# Revit family: QF_ELECTROLUXPROFESSIONAL_1LSN7S_WB6-20_E
name_source: partatom
category: Attrezzature speciali
units: mm (PartAtom-declared; Revit-internal decimal feet)

## family parameters
Basato su piano di lavoro = No
Condiviso = No
Punto di calcolo locali = No
Quota connettore circolare = Usa diametro
Sempre verticale = Sì
Taglio con vuoti quando caricato = No
Tipo di parte = Normale

## types (108) — shared parameters
Cold Water Maximum Pressure = 0.00 psi
Cold Water Minimum Pressure = 0.00 psi
Cold Water Size = 1"
Conn Conduit = Sì
Depth Actual = 1050 mm
Electrical Remarks = 400 V/3N ph/50/60 Hz
Height Actual = 1640 mm  [stored 5.38058 ft]
Hot Water Consumption = 0 GPM
Hot Water Maximum Pressure = 0.00 psi
Hot Water Minimum Pressure = 0.00 psi
Hot Water Size = 1"
Hot Water Temperature = -460 °F
Indirect Waste Size = 1"
Latent Heat Output = 0.0
Length Actual = 915 mm  [stored 3.00197 ft]
Max Overcurrent Protection = 0 A
Min Ckt Ampacity = 0 A
Modello = WB6-20
Phase = 3
Produttore = Electrolux Professional
Sensible Heat Output = 0.0
URL = www.electroluxprofessional.com
Weight = 670
Weight in Pounds = 55.1
zero-valued in all types: Cold Water Connection Height, Gas KW, Hot Water Connection Height, Indirect Waste Connection Height, Prospetto di default, Steam Pounds per Hour

## per-type parameters (varying)
| type | Descrizione | Volts | Watts |
| 9890030056 | WASHER WB6-20 200L 2DOORS RIGHT/RIGHT EL. 380-415/50/60/3 2xCOMPASS PRO 2xWATER 13xLIQ. SILVER TAP BMP | 415 V | 15000 W |
| 9890030096 | WASHER WB6-20 200L 2DOORS RIGHT/RIGHT EL. 380-415/50/60/3 COMPASS PRO 2xWATER 13xLIQ. SILVER IWS TAP EXP. | 415 V | 15000 W |
| 9890030086 | WASHER WB6-20 200L 2DOORS RIGHT/RIGHT EL. 380-415/50/60/3 2xCOMPASS PRO 2xWATER 13xLIQ. SST IWS | 415 V | 15000 W |
| 9890030052 | WASHER WB6-20 200L 2DOORS RIGHT/LEFT EL. 380-415/50/60/3 COMPASS PRO 2xWATER 13xLIQ. SILVER EXP. | 415 V | 15000 W |
| 9890030042 | WASHER WB6-20 200L 2DOORS RIGHT/RIGHT EL. 380-415/50/60/3 COMPASS PRO 3xWATER 13xLIQ.+POWDER SILVER BMP | 415 V | 15000 W |
| 9890030072 | WASHER WB6-20 200L 2DOORS LEFT/RIGHT EL. 380-415/50/60/3 COMPASS PRO 2xWATER 13xLIQ. SILVER TAP ALARM EXP. | 415 V | 15000 W |
| 9890030062 | WASHER WB6-20 200L 2DOORS RIGHT/RIGHT EL. 380-415/50/60/3 2xCOMPASS PRO 3xWATER 13xLIQ. SILVER TAP ALARM | 415 V | 15000 W |
| 9890030012 | WASHER WB6-20 200L 2DOORS RIGHT/RIGHT EL. 230/50/60/3 2xCOMPASS PRO 2xWATER 13xLIQ. SILVER AIDO TAP ALARM EXP. | 230 V | 15000 W |
| 9890030002 | WASHER WB6-20 200L 2DOORS RIGHT/RIGHT EL. 380-415/50/60/3 2xCOMPASS PRO 3xWATER 13xLIQ. SILVER ALARM EXP. | 415 V | 15000 W |
| 9890030032 | WASHER WB6-20 200L 2DOORS RIGHT/RIGHT EL. 380-415/50/60/3 COMPASS PRO 3xWATER 13xLIQ. SILVER | 415 V | 15000 W |
| 9890030022 | WASHER WB6-20 200L 2DOORS RIGHT/RIGHT EL. 230/50/60/3 2xCOMPASS PRO 2xWATER 13xLIQ. SILVER TAP ALARM EXP. | 230 V | 15000 W |
| 9890030082 | WASHER WB6-20 200L 2DOORS RIGHT/RIGHT EL. 380-415/50/60/3 2xCOMPASS PRO 2xWATER 13xLIQ.+POWDER SILVER EXP. | 415 V | 15000 W |
| 9890030114 | WASHER WB6-20 200L 2DOORS LEFT/LEFT EL. 380-415/50/60/3 COMPASS PRO 3xWATER 13xLIQ.+POWDER SILVER IWS ALARM EXP. | 415 V | 15000 W |
| 9890030104 | WASHER WB6-20 200L 2DOORS RIGHT/RIGHT EL. 380-415/50/60/3 2xCOMPASS PRO 3xWATER 13xLIQ.+POWDER SILVER AIDO TAP ALARM EXP | 415 V | 15000 W |
| 9890030079 | WASHER WB6-20 200L 2DOORS LEFT/RIGHT EL. 380-415/50/60/3 COMPASS PRO 2xWATER 13xLIQ. SILVER ALARM | 415 V | 15000 W |
| 9890030049 | WASHER WB6-20 200L 2DOORS RIGHT/RIGHT EL. 380-415/50/60/3 2xCOMPASS PRO 3xWATER 13xLIQ. SILVER AIDO ALARM | 415 V | 15000 W |
| 9890030019 | WASHER WB6-20 200L 2DOORS LEFT/LEFT EL. 380-415/50/60/3 COMPASS PRO 2xWATER 13xLIQ. SILVER | 415 V | 15000 W |
| 9890030009 | WASHER WB6-20 200L 2DOORS RIGHT/RIGHT EL. 380-415/50/60/3 2xCOMPASS PRO 2xWATER 13xLIQ. SILVER EXP. | 415 V | 15000 W |
| 9890030039 | WASHER WB6-20 200L 2DOORS RIGHT/LEFT EL. 380-415/50/60/3 2xCOMPASS PRO 2xWATER 13xLIQ. SILVER ALARM EXP. | 415 V | 15000 W |
| 9890030059 | WASHER WB6-20 200L 2DOORS RIGHT/RIGHT EL. 380-415/50/60/3 2xCOMPASS PRO 3xWATER 13xLIQ.+POWDER SILVER | 415 V | 15000 W |
| 9890030069 | WASHER WB6-20 200L 2DOORS LEFT/RIGHT EL. 380-415/50/60/3 COMPASS PRO 3xWATER 13xLIQ.+POWDER SILVER EXP. | 415 V | 15000 W |
| 9890030099 | WASHER WB6-20 200L 2DOORS RIGHT/RIGHT EL. 380-415/50/60/3 2xCOMPASS PRO 2xWATER 13xLIQ. SILVER AIDO IWS TAP ALARM EXP. | 415 V | 15000 W |
| 9890030089 | WASHER WB6-20 200L 2DOORS RIGHT/RIGHT EL. 380-415/50/60/3 COMPASS PRO 2xWATER 13xLIQ.+POWDER SILVER ALARM EXP. | 415 V | 15000 W |
| 9890030055 | WASHER WB6-20 200L 2DOORS RIGHT/RIGHT NO HEATING 380-415/50/60/3 COMPASS PRO 2xWATER 13xLIQ. SILVER | 415 V | 6000 W |
| 9890030045 | WASHER WB6-20 200L 2DOORS RIGHT/RIGHT EL. 380-415/50/60/3 2xCOMPASS PRO 3xWATER 13xLIQ. SILVER AIDO | 415 V | 15000 W |
| 9890030075 | WASHER WB6-20 200L 2DOORS RIGHT/RIGHT EL. 380-415/50/60/3 2xCOMPASS PRO 2xWATER 13xLIQ. SILVER AIDO ALARM | 415 V | 15000 W |
| 9890030065 | WASHER WB6-20 200L 2DOORS RIGHT/RIGHT EL. 380-415/50/60/3 2xCOMPASS PRO 2xWATER 13xLIQ.+POWDER SILVER TAP ALARM | 415 V | 15000 W |
| 9890030015 | WASHER WB6-20 200L 2DOORS RIGHT/RIGHT EL. 380-415/50/60/3 2xCOMPASS PRO 2xWATER 13xLIQ. SILVER AIDO | 415 V | 15000 W |
| 9890030005 | WASHER WB6-20 200L 2DOORS RIGHT/RIGHT EL. 380-415/50/60/3 COMPASS PRO 2xWATER 13xLIQ. SILVER | 415 V | 15000 W |
| 9890030035 | WASHER WB6-20 200L 2DOORS RIGHT/RIGHT EL. 380-415/50/60/3 COMPASS PRO 2xWATER 13xLIQ.+POWDER SILVER | 415 V | 15000 W |
| 9890030025 | WASHER WB6-20 200L 2DOORS LEFT/RIGHT EL. 380-415/50/60/3 COMPASS PRO 2xWATER 13xLIQ. SILVER TAP EXP. | 415 V | 15000 W |
| 9890030100 | WASHER WB6-20 200L 2DOORS RIGHT/RIGHT EL. 380-415/50/60/3 2xCOMPASS PRO 2xWATER 13xLIQ. SILVER IWS ALARM | 415 V | 15000 W |
| 9890030110 | WASHER WB6-20 200L 2DOORS RIGHT/RIGHT EL. 380-415/50/60/3 COMPASS PRO 2xWATER 13xLIQ. SILVER IWS | 415 V | 15000 W |
| 9890030085 | WASHER WB6-20 200L 2DOORS RIGHT/RIGHT EL. 380-415/50/60/3 2xCOMPASS PRO 2xWATER 13xLIQ.+POWDER SILVER ALARM EXP. | 415 V | 15000 W |
| 9890030058 | WASHER WB6-20 200L 2DOORS RIGHT/RIGHT EL. 380-415/50/60/3 2xCOMPASS PRO 2xWATER 13xLIQ. SILVER IWS ALARM BMP EXP. | 415 V | 15000 W |
| 9890030048 | WASHER WB6-20 200L 2DOORS LEFT/RIGHT EL. 380-415/50/60/3 2xCOMPASS PRO 2xWATER 13xLIQ.+POWDER SILVER | 415 V | 15000 W |
| 9890030078 | WASHER WB6-20 200L 2DOORS RIGHT/RIGHT EL. 380-415/50/60/3 2xCOMPASS PRO 2xWATER 13xLIQ.+POWDER SILVER IWS BMP | 415 V | 15000 W |
| 9890030068 | WASHER WB6-20 200L 2DOORS RIGHT/RIGHT EL. 380-415/50/60/3 2xCOMPASS PRO 2xWATER 13xLIQ. SILVER ALARM | 415 V | 15000 W |
| 9890030018 | WASHER WB6-20 200L 2DOORS LEFT/RIGHT EL. 380-415/50/60/3 COMPASS PRO 2xWATER 13xLIQ. SILVER | 415 V | 15000 W |
| 9890030008 | WASHER WB6-20 200L 2DOORS RIGHT/RIGHT EL. 380-415/50/60/3 2xCOMPASS PRO 2xWATER 13xLIQ. SILVER ALARM EXP. | 415 V | 15000 W |
| 9890030038 | WASHER WB6-20 200L 2DOORS LEFT/LEFT EL. 380-415/50/60/3 2xCOMPASS PRO 3xWATER 13xLIQ.+POWDER 2xDRAIN SILVER TAP ALARM EX | 415 V | 15000 W |
| 9890030028 | WASHER WB6-20 200L 2DOORS RIGHT/RIGHT EL. 380-415/50/60/3 COMPASS PRO 2xWATER 13xLIQ.+POWDER SILVER EXP. | 415 V | 15000 W |
| 9890030115 | WASHER WB6-20 200L 2DOORS RIGHT/RIGHT EL. 380-415/50/60/3 2xCOMPASS PRO 2xWATER 13xLIQ. SILVER ALARM BMP EXP. | 415 V | 15000 W |
| 9890030098 | WASHER WB6-20 200L 2DOORS RIGHT/RIGHT EL. 380-415/50/60/3 2xCOMPASS PRO 3xWATER 13xLIQ.+POWDER SST IWS ALARM EXP. | 415 V | 15000 W |
| 9890030088 | WASHER WB6-20 200L 2DOORS RIGHT/RIGHT EL. 380-415/50/60/3 COMPASS PRO 2xWATER 13xLIQ.+POWDER SILVER EXP. | 415 V | 15000 W |
| 9890030051 | WASHER WB6-20 200L 2DOORS LEFT/LEFT EL. 380-415/50/60/3 2xCOMPASS PRO 2xWATER 13xLIQ.+POWDER SST ALARM EXP. | 415 V | 15000 W |
| 9890030071 | WASHER WB6-20 200L 2DOORS RIGHT/LEFT EL. 380-415/50/60/3 COMPASS PRO 2xWATER 13xLIQ. SILVER TAP ALARM EXP. | 415 V | 15000 W |
| 9890030061 | WASHER WB6-20 200L 2DOORS RIGHT/RIGHT EL. 380-415/50/60/3 2xCOMPASS PRO 3xWATER 13xLIQ.+POWDER SILVER AIDO ALARM EXP. | 415 V | 15000 W |
| 9890030011 | WASHER WB6-20 200L 2DOORS RIGHT/RIGHT EL. 230/50/60/3 2xCOMPASS PRO 2xWATER 13xLIQ. SILVER TAP ALARM EXP. | 230 V | 15000 W |
| 9890030001 | WB6-20 EL GR CP 400/3/50 | 415 V | 15000 W |
| 9890030031 | WASHER WB6-20 200L 2DOORS RIGHT/RIGHT NO HEATING 380-415/50/60/3 2xCOMPASS PRO 3xWATER 13xLIQ. 2xDRAIN SILVER AIDO TAP A | 415 V | 6000 W |
| 9890030021 | WASHER WB6-20 200L 2DOORS RIGHT/RIGHT EL. 380-415/50/60/3 2xCOMPASS PRO 2xWATER 13xLIQ.+POWDER SILVER IWS ALARM EXP. | 415 V | 15000 W |
| 9890030081 | WASHER WB6-20 200L 2DOORS RIGHT/RIGHT EL. 380-415/50/60/3 2xCOMPASS PRO 2xWATER 13xLIQ. SILVER IWS | 415 V | 15000 W |
| 9890030091 | WASHER WB6-20 200L 2DOORS RIGHT/RIGHT EL. 380-415/50/60/3 2xCOMPASS PRO 2xWATER 13xLIQ.+POWDER SST AIDO ALARM EXP. | 415 V | 15000 W |
| 9890030054 | WASHER WB6-20 200L 2DOORS RIGHT/LEFT EL. 380-415/50/60/3 2xCOMPASS PRO 2xWATER 13xLIQ. SILVER | 415 V | 15000 W |
| 9890030044 | WASHER WB6-20 200L 2DOORS RIGHT/LEFT EL. 380-415/50/60/3 COMPASS PRO 3xWATER 13xLIQ. SILVER | 415 V | 15000 W |
| 9890030074 | WASHER WB6-20 200L 2DOORS RIGHT/RIGHT EL. 380-415/50/60/3 2xCOMPASS PRO 2xWATER 13xLIQ. SILVER AIDO IWS ALARM EXP. | 415 V | 15000 W |
| 9890030064 | WASHER WB6-20 200L 2DOORS RIGHT/RIGHT EL. 380-415/50/60/3 2xCOMPASS PRO 2xWATER 13xLIQ. SILVER TAP ALARM | 415 V | 15000 W |
| 9890030014 | WASHER WB6-20 200L 2DOORS RIGHT/RIGHT EL. 380-415/50/60/3 2xCOMPASS PRO 2xWATER 13xLIQ. SILVER AIDO TAP ALARM EXP. | 415 V | 15000 W |
| 9890030004 | WASHER WB6-20 200L 2DOORS LEFT/RIGHT EL. 380-415/50/60/3 COMPASS PRO 2xWATER 13xLIQ.+POWDER SILVER EXP. | 415 V | 15000 W |
| 9893030002 | WASHER WB6-20 200L 2DOORS RIGHT/RIGHT NO HEATING 208-240/50/60/3 COMPASS PRO 2xWATER 13xLIQ.+POWDER SILVER ALARM EXP. ET | 240 V | 6000 W |
| 9890030024 | WASHER WB6-20 200L 2DOORS RIGHT/RIGHT NO HEATING 380-415/50/60/3 2xCOMPASS PRO 3xWATER 13xLIQ. 2xDRAIN SILVER AIDO TAP A | 415 V | 6000 W |
| 9890030101 | WASHER WB6-20 200L 2DOORS RIGHT/RIGHT EL. 380-415/50/60/3 COMPASS PRO 2xWATER 13xLIQ. SILVER TAP ALARM | 415 V | 15000 W |
| 9890030084 | WASHER WB6-20 200L 2DOORS RIGHT/RIGHT EL. 380-415/50/60/3 COMPASS PRO 2xWATER 13xLIQ. SILVER TAP ALARM EXP. | 415 V | 15000 W |
| 9890030050 | WASHER WB6-20 200L 2DOORS RIGHT/LEFT EL. 380-415/50/60/3 COMPASS PRO 2xWATER 13xLIQ.+POWDER SILVER EXP. | 415 V | 15000 W |
| 9890030040 | WASHER WB6-20 200L 2DOORS RIGHT/RIGHT EL. 380-415/50/60/3 2xCOMPASS PRO 2xWATER 13xLIQ. SILVER ALARM EXP. | 415 V | 15000 W |
| 9890030070 | WASHER WB6-20 200L 2DOORS RIGHT/LEFT EL. 380-415/50/60/3 2xCOMPASS PRO 2xWATER 13xLIQ. SILVER ALARM EXP. | 415 V | 15000 W |
| 9890030060 | WASHER WB6-20 200L 2DOORS LEFT/LEFT EL. 380-415/50/60/3 2xCOMPASS PRO 2xWATER 13xLIQ.+POWDER SILVER | 415 V | 15000 W |
| 9890030010 | WASHER WB6-20 200L 2DOORS RIGHT/RIGHT EL. 380-415/50/60/3 COMPASS PRO 3xWATER 13xLIQ.+POWDER SILVER EXP. | 415 V | 15000 W |
| 9890030030 | WASHER WB6-20 200L 2DOORS RIGHT/RIGHT EL. 380-415/50/60/3 2xCOMPASS PRO 3xWATER 13xLIQ.+POWDER 2xDRAIN SILVER AIDO TAP A | 415 V | 15000 W |
| 9890030020 | WASHER WB6-20 200L 2DOORS LEFT/RIGHT EL. 380-415/50/60/3 COMPASS PRO 2xWATER 13xLIQ. SILVER EXP. | 415 V | 15000 W |
| 9890030080 | WASHER WB6-20 200L 2DOORS LEFT/RIGHT EL. 380-415/50/60/3 2xCOMPASS PRO 2xWATER 13xLIQ. SILVER TAP ALARM EXP. | 415 V | 15000 W |
| 9893030003 | WASHER WB6-20 200L 2DOORS RIGHT/RIGHT EL. 208-240/50/60/3 COMPASS PRO 2xWATER 13xLIQ.+POWDER SILVER ALARM EXP. ETL | 240 V | 15000 W |
| 9891030001 | WASHER WB6-20 200L 1DOOR RIGHT EL. 380-415/50/60/3 COMPASS PRO 2xWATER 13xLIQ.+POWDER SILVER | 415 V | 15000 W |
| 9890030109 | WASHER WB6-20 200L 2DOORS RIGHT/RIGHT EL. 380-415/50/60/3 2xCOMPASS PRO 2xWATER 13xLIQ.+POWDER SILVER | 415 V | 15000 W |
| 9891030002 | WASHER WB6-20 200L 1DOOR RIGHT EL. 380-415/50/60/3 COMPASS PRO 2xWATER 13xLIQ. SILVER | 415 V | 15000 W |
| 9893030001 | WASHER WB6-20 200L 2DOORS RIGHT/RIGHT NO HEATING 208-240/50/60/3 COMPASS PRO 2xWATER 13xLIQ.+POWDER SST ALARM EXP. ETL | 240 V | 6000 W |
| 9890030116 | WASHER WB6-20 200L 2DOORS RIGHT/RIGHT EL. 380-415/50/60/3 2xCOMPASS PRO 3xWATER 13xLIQ. SST TAP ALARM EXP. | 415 V | 15000 W |
| 9890030106 | WASHER WB6-20 200L 2DOORS RIGHT/RIGHT EL. 380-415/50/60/3 2xCOMPASS PRO 2xWATER 13xLIQ. SST AIDO IWS TAP ALARM EXP. | 415 V | 15000 W |
| 9890030057 | WASHER WB6-20 200L 2DOORS RIGHT/RIGHT EL. 380-415/50/60/3 2xCOMPASS PRO 2xWATER 13xLIQ. SILVER ALARM BMP EXP. | 415 V | 15000 W |
| 9890030047 | WASHER WB6-20 200L 2DOORS RIGHT/LEFT EL. 380-415/50/60/3 2xCOMPASS PRO 2xWATER 13xLIQ.+POWDER SILVER | 415 V | 15000 W |
| 9890030077 | WASHER WB6-20 200L 2DOORS RIGHT/RIGHT EL. 380-415/50/60/3 COMPASS PRO 3xWATER 13xLIQ. SILVER EXP. | 415 V | 15000 W |
| 9890030102 | WASHER WB6-20 200L 2DOORS RIGHT/RIGHT EL. 380-415/50/60/3 2xCOMPASS PRO 3xWATER 13xLIQ. SILVER AIDO TAP ALARM EXP. | 415 V | 15000 W |
| 9890030017 | WASHER WB6-20 200L 2DOORS RIGHT/LEFT EL. 380-415/50/60/3 COMPASS PRO 2xWATER 13xLIQ. SILVER | 415 V | 15000 W |
| 9890030037 | WASHER WB6-20 200L 2DOORS RIGHT/RIGHT EL. 380-415/50/60/3 COMPASS PRO 2xWATER 13xLIQ. SILVER EXP. | 415 V | 15000 W |
| 9890030027 | WASHER WB6-20 200L 2DOORS RIGHT/RIGHT EL. 380-415/50/60/3 2xCOMPASS PRO 2xWATER 13xLIQ. SILVER EXP. | 415 V | 15000 W |
| 9890030112 | WASHER WB6-20 200L 2DOORS LEFT/LEFT EL. 380-415/50/60/3 COMPASS PRO 2xWATER 13xLIQ.+POWDER SILVER | 415 V | 15000 W |
| 9890030097 | WASHER WB6-20 200L 2DOORS RIGHT/RIGHT EL. 380-415/50/60/3 2xCOMPASS PRO 2xWATER 13xLIQ.+POWDER SILVER AIDO ALARM | 415 V | 15000 W |
| 9890030087 | WASHER WB6-20 200L 2DOORS RIGHT/RIGHT EL. 380-415/50/60/3 2xCOMPASS PRO 2xWATER 13xLIQ. SILVER IWS EXP. | 415 V | 15000 W |
| 9890030107 | WASHER WB6-20 200L 2DOORS RIGHT/RIGHT EL. 380-415/50/60/3 2xCOMPASS PRO 3xWATER 13xLIQ. SILVER ALARM | 415 V | 15000 W |
| 9890030053 | WASHER WB6-20 200L 2DOORS RIGHT/RIGHT EL. 380-415/50/60/3 2xCOMPASS PRO 2xWATER 13xLIQ.+POWDER SILVER AIDO | 415 V | 15000 W |
| 9890030043 | WASHER WB6-20 200L 2DOORS RIGHT/RIGHT EL. 380-415/50/60/3 2xCOMPASS PRO 2xWATER 13xLIQ.+POWDER SILVER ALARM BMP | 415 V | 15000 W |
| 9890030073 | WASHER WB6-20 200L 2DOORS RIGHT/LEFT EL. 380-415/50/60/3 COMPASS PRO 2xWATER 13xLIQ. SILVER ALARM | 415 V | 15000 W |
| 9890030063 | WASHER WB6-20 200L 2DOORS LEFT/LEFT EL. 380-415/50/60/3 COMPASS PRO 2xWATER 13xLIQ.+POWDER SILVER EXP. | 415 V | 15000 W |
| 9890030013 | WASHER WB6-20 200L 2DOORS RIGHT/RIGHT EL. 380-415/50/60/3 2xCOMPASS PRO 2xWATER 13xLIQ. SILVER TAP ALARM EXP. | 415 V | 15000 W |
| 9890030003 | WASHER WB6-20 200L 2DOORS RIGHT/RIGHT EL. 380-415/50/60/3 2xCOMPASS PRO 2xWATER 13xLIQ. SILVER | 415 V | 15000 W |
| 9890030033 | WASHER WB6-20 200L 2DOORS LEFT/RIGHT EL. 380-415/50/60/3 COMPASS PRO 3xWATER 13xLIQ. SILVER | 415 V | 15000 W |
| 9890030023 | WASHER WB6-20 200L 2DOORS RIGHT/RIGHT EL. 380-415/50/60/3 2xCOMPASS PRO 3xWATER 13xLIQ.+POWDER 2xDRAIN SILVER AIDO TAP A | 415 V | 15000 W |
| 9890030093 | WASHER WB6-20 200L 2DOORS RIGHT/RIGHT EL. 380-415/50/60/3 2xCOMPASS PRO 3xWATER 13xLIQ. 2xDRAIN SILVER ALARM | 415 V | 15000 W |
| 9890030083 | WASHER WB6-20 200L 2DOORS LEFT/RIGHT EL. 380-415/50/60/3 2xCOMPASS PRO 2xWATER 13xLIQ.+POWDER SILVER ALARM | 415 V | 15000 W |
| 9890030113 | WASHER WB6-20 200L 2DOORS RIGHT/RIGHT EL. 380-415/50/60/3 COMPASS PRO 2xWATER 13xLIQ. SILVER ALARM | 415 V | 15000 W |
| 9890030103 | WASHER WB6-20 200L 2DOORS RIGHT/LEFT EL. 380-415/50/60/3 2xCOMPASS PRO 3xWATER 13xLIQ. SILVER TAP ALARM EXP. | 415 V | 15000 W |
| 9890030046 | WASHER WB6-20 200L 2DOORS LEFT/RIGHT EL. 380-415/50/60/3 2xCOMPASS PRO 2xWATER 13xLIQ. SILVER | 415 V | 15000 W |
| 9890030076 | WASHER WB6-20 200L 2DOORS RIGHT/RIGHT EL. 380-415/50/60/3 COMPASS PRO 3xWATER 13xLIQ. SILVER IWS | 415 V | 15000 W |
| 9890030016 | WASHER WB6-20 200L 2DOORS RIGHT/RIGHT EL. 380-415/50/60/3 COMPASS PRO 2xWATER 13xLIQ.+POWDER SILVER IWS | 415 V | 15000 W |
| 9890030006 | WASHER WB6-20 200L 2DOORS RIGHT/RIGHT EL. 380-415/50/60/3 2xCOMPASS PRO 2xWATER 13xLIQ.+POWDER SILVER | 415 V | 15000 W |
| 9890030036 | WASHER WB6-20 200L 2DOORS RIGHT/RIGHT EL. 380-415/50/60/3 2xCOMPASS PRO 2xWATER 13xLIQ. SILVER AIDO IWS TAP ALARM BMP EX | 415 V | 15000 W |
| 9890030026 | WASHER WB6-20 200L 2DOORS RIGHT/RIGHT EL. 380-415/50/60/3 2xCOMPASS PRO 2xWATER 13xLIQ. SILVER AIDO IWS TAP ALARM BMP EX | 415 V | 15000 W |

note: [stored X ft] marks values corroborated as IEEE doubles in the binary element streams (Revit-internal decimal feet)

## geometry (parser evidence)
native form markers: Blend x4, Sweep x3
no freeform markers — native parametric forms only
